# Revit family: Remeha_GasAce120-65_LOD-3
name_source: partatom
category: Mechanical Equipment
revit_build: Autodesk Revit 2017 (Build: 20190508_0315(x64)
units: mm (PartAtom-declared; Revit-internal decimal feet)

## family parameters
Always vertical = Yes
Cut with Voids When Loaded = No
OmniClass Number = 23.75.10.11.14
OmniClass Title = Hot Water Heat Generators
Part Type = Normal
Room Calculation Point = No
Round Connector Dimension = Use Diameter
Shared = No
Work Plane-Based = No

## types (1)
- Gas Ace 120 - 65
    6 Monthly = 0
    Access Clearance Bottom = 0.00 mm
    Access Clearance Front = 500.00 mm
    Access Clearance Left = 500.00 mm
    Access Clearance Rear = 350.00 mm
    Access Clearance Right = 500.00 mm
    Access Clearance Top = 500.00 mm
    Air Inlet Connection Size = 150.00 mm
    Annually = As per attached URL O & M Manual
    BMS Links = Yes
    Bespoke Timeframe = 0
    Building Regulations Seasonal Efficiency = 97.6 %
    Burner Control Type = Modulating
    CE Mark = 0085CT0009
    Colour = RAL 9016
    Condensate Drain Size = 22.00 mm
    Condensate Drain Type = Plain
    Configuration = Single boiler
    Control Type = R-Bus,0 - 10V, Open Therm, Volt free enable, Direct boiler weather compensating control systems available from Remeha as optional extra's.
    Daily = 0
    Drain Connection Size = 0.00 mm
    Drain Connection Type = Unset
    Energy Technology List = 0
    ErP Energy Label = A
    ErP Rated Efficiency at Full Load = 89.4  %
    ErP Rated Efficiency at Part Load = 99.5 %
    ErP Seasonal Efficiency = 94 %
    Expected Life = 15
    External Material = Steel
    Features = Remeha's Gas 120 range are compact high efficiency floor standing condensing boilers. Lighter and more efficienct, their small size make them ideally suited to modular arrangments
    Finish = High Polish Gardner 60 GRAD 91EH
    Flow and Return Connection Size = 32.00 mm
    Flow and Return Connection Type = Threaded
    Flue Connection size = 100.00 mm
    Flue or Air Intake Classification = B23,B23P,B33,C13,C33,C43,C53,C63,C83,C93
    Frequency = 50 Hz
    Fuel Connection Size = 20.00 mm
    Fuel Connection Type = Threaded
    Full Load Current = 0 A
    Fuse Rating = 10 A
    Gas Consumption rate = 6.6 m3/h
    Gross Weight = 98.00 kg
    Heat Exchanger Material = Aluminium
    Heater Operation = Condensing
    Hydraulic Resistance at 11C temperature differential = 0.562
    Hydraulic Resistance at 20C temperature differential = 0.170
    IK Rating = 0
    IP Rating = IPX1B
    IfcExportAs = IfcBoilerType
    IfcExportType = NOTDEFINED
    Interlocks = Yes
    Maintenance Required 0 to 300hrs = 0
    Maintenance Required 1001 to 2000hrs = 0
    Maintenance Required 2001 to 4000hrs = 0
    Maintenance Required 301 to 600hrs = 0
    Maintenance Required 4001 to 8000hrs = 0
    Maintenance Required 601 to 1000hrs = 0
    Maintenance Required 8001 to 12000hrs = 0
    Manufacturer = Remeha Commercial
    Manufacturer Website = https://www.remeha.co.uk
    Maximum Gas Inlet Pressure = 0.025 bar
    Maximum Oil Inlet Pressure = 0.000 bar
    Maximum Operating Pressure = 4.000 bar
    Maximum Power Consumption = 92 W
    Minimum Flow Rate at 11C temperature differential = 1.3 L/s
    Minimum Flow Rate at 20C temperature differential = 0.7 L/s
    Minimum Gas Inlet Pressure = 0.017 bar
    Minimum Oil Inlet Pressure = 0.000 bar
    Minimum Operating Pressure = 0.800 bar
    Minimum Power Consumption = 25 W
    Monthly = 0
    Mounting = Floor Standing
    NOx Emissions = 32 mg/kWh
    Nominal Gas Inlet Pressure = 0.017 bar
    Nominal Oil Inlet Pressure = 0.000 bar
    Oil Consumption rate = 0
    Operation and Maintenance Manual = https://www.remeha.co.uk
    Optional Fuel = Gas - LPG
    Overall Height = 1340.00 mm
    Overall Length = 605.00 mm
    Overall Width = 600.00 mm
    Primary Fuel = Gas - NG
    Product Literature = https://www.remeha.co.uk
    Product Model Number = 7721607
    Product Range = Gas 120 - 65kW
    Quarterly = 0
    Rated Criteria = 80/60
    Rated Output = 61500 W
    Reference Standard = (EU) 2016/426 92/42/EEC 2009/125/EC
    Safety Valve Connection Size = 0.00 mm
    Safety Valve Connection Type = Unset
    Shape = Rectangular (Vertical)
    Shipping Weight = 0.00 kg
    Sound Pressure Level = 40 dBA
    Starting Current = 0 A
    Supply Phase = 1
    Turndown Ratio = 5.08:1
    Type = Space heating
    Uniclass2015 = Pr_60_60_08
    Voltage = 230 V
    Water Content = 7.1 L
    Water Treatment Required = Yes
    Weekly = 0

note: source unit labels omitted for Hydraulic Resistance at 11C temperature differential, Hydraulic Resistance at 20C temperature differential — the stored unit's dimension contradicts the parameter name (converter mislabeling)

## geometry (parser evidence)
native form markers: Blend x13, Sweep x4
no freeform markers — native parametric forms only
